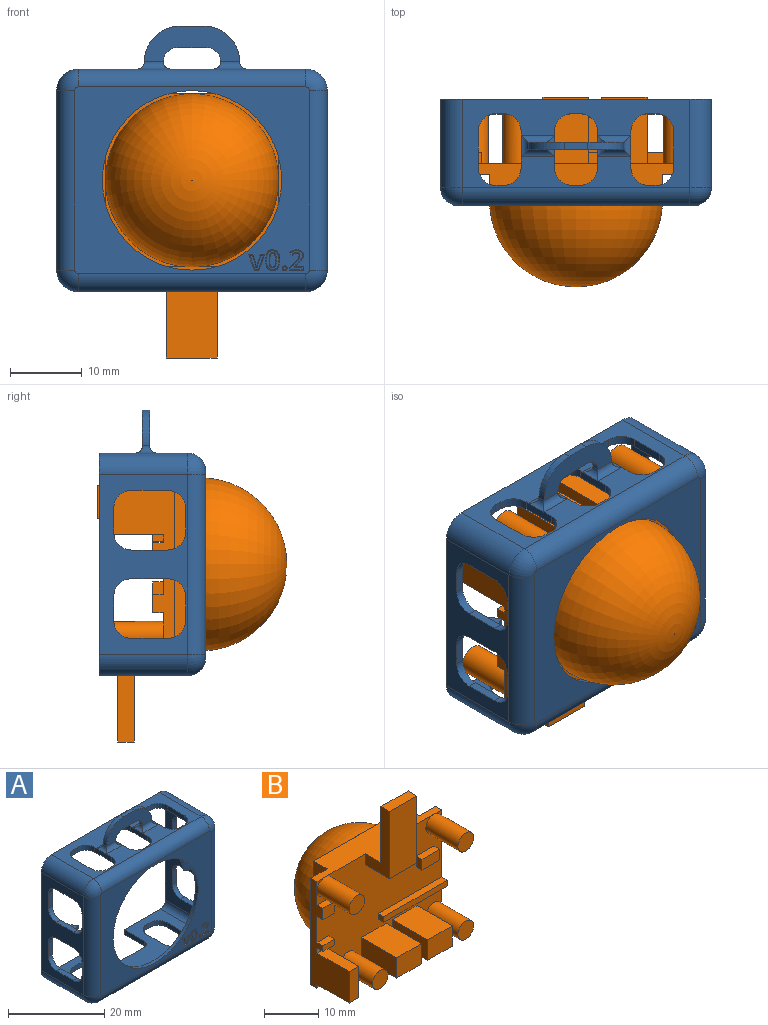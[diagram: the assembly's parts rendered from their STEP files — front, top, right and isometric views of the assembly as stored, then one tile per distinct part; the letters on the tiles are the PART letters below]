
ASSEMBLY  parts=2 mates=2
PART A: 200 faces, bbox 37.9x15x37.2 mm
  f0: plane 32.86x26.2mm, normal (0,-1,0), area 350.2mm2, adj f18,f129,f130,f131,f132,f133,f134,f135
  f1: plane 31.7x12.3mm, normal (0,0,1), area 198.1mm2, adj f9,f10,f17,f65,f66,f67,f68,f69
  f2: plane 32.3x12.5mm, normal (0,0,1), area 217.7mm2, adj f12,f13,f17,f20,f21,f22,f23,f24
  f3: plane 31.7x12.3mm, normal (0,0,-1), area 203.9mm2, adj f11,f16,f17,f20,f21,f22,f23,f24
  f4: plane 32.3x12.5mm, normal (0,0,-1), area 239.8mm2, adj f14,f15,f17,f65,f66,f67,f68,f69
  f5: plane 25.64x12.5mm, normal (1,0,0), area 156.8mm2, adj f13,f14,f17,f25,f26,f27,f28,f49
  f6: plane 25.04x12.3mm, normal (1,0,0), area 152.3mm2, adj f9,f16,f17,f33,f34,f35,f36,f37
  f7: plane 25.04x12.3mm, normal (-1,0,0), area 152.3mm2, adj f10,f11,f17,f49,f50,f51,f52,f53
  f8: plane 25.64x12.5mm, normal (-1,0,0), area 156.8mm2, adj f12,f15,f17,f29,f30,f31,f32,f33
  f9: cylinder r=3mm len=12.3mm, axis (0,-1,0), area 58mm2, adj f1,f6,f17,f134
  f10: cylinder r=3mm len=12.3mm, axis (0,-1,0), area 58mm2, adj f1,f7,f17,f130
  f11: cylinder r=3mm len=12.3mm, axis (0,-1,0), area 58mm2, adj f3,f7,f17,f131
  f12: cylinder r=1.5mm len=12.5mm, axis (0,-1,0), area 29.5mm2, adj f2,f8,f17,f126
  f13: cylinder r=1.5mm len=12.5mm, axis (0,-1,0), area 29.5mm2, adj f2,f5,f17,f127
  f14: cylinder r=1.5mm len=12.5mm, axis (0,-1,0), area 29.5mm2, adj f4,f5,f17,f123
  f15: cylinder r=1.5mm len=12.5mm, axis (0,-1,0), area 29.5mm2, adj f4,f8,f17,f122
  f16: cylinder r=3mm len=12.3mm, axis (0,-1,0), area 58mm2, adj f3,f6,f17,f135
  f17: plane 37.7x31.04mm, normal (0,1,0), area 140.8mm2, adj f1,f2,f3,f4,f5,f6,f7,f8
  f18: cylinder r=12.5mm len=25mm, axis (0,1,0), area 62.8mm2, adj f0,f19
  f19: plane 32.3x25.64mm, normal (0,1,0), area 337.3mm2, adj f18,f121,f124,f125,f128
  f20: plane 5.9x1.2mm, normal (-1,0,0), area 7.1mm2, adj f2,f3,f17,f21
  f21: cylinder r=1.5mm len=1.5mm, axis (0,0,-1), area 2.8mm2, adj f2,f3,f20,f22
  f22: plane 7.5x1.2mm, normal (0,1,0), area 9mm2, adj f2,f3,f21,f23
  f23: cylinder r=1.5mm len=1.5mm, axis (0,0,-1), area 2.8mm2, adj f2,f3,f22,f24
  f24: plane 5.9x1.2mm, normal (1,0,0), area 7.1mm2, adj f2,f3,f17,f23
  f25: plane 2.2x2mm, normal (0.41,-0.91,0), area 4.8mm2, adj f5,f26,f27,f28
  f26: plane 3x2.2mm, normal (0.81,0.59,0), area 7.4mm2, adj f5,f25,f27,f28
  f27: plane 4x2.2mm, normal (0,0,-1), area 4.4mm2, adj f5,f25,f26
  f28: plane 4x2.2mm, normal (0,0,1), area 4.4mm2, adj f5,f25,f26
  f29: plane 3x2.2mm, normal (-0.81,0.59,0), area 7.4mm2, adj f8,f30,f31,f32
  f30: plane 2.2x2mm, normal (-0.41,-0.91,0), area 4.8mm2, adj f8,f29,f31,f32
  f31: plane 4x2.2mm, normal (0,0,1), area 4.4mm2, adj f8,f29,f30
  f32: plane 4x2.2mm, normal (0,0,-1), area 4.4mm2, adj f8,f29,f30
  f33: plane 3.32x1.2mm, normal (0,-1,0), area 4mm2, adj f6,f8,f34,f40
  f34: cylinder r=2.5mm len=2.5mm, axis (1,0,0), area 4.7mm2, adj f6,f8,f33,f35
  f35: plane 5x1.2mm, normal (0,0,1), area 6mm2, adj f6,f8,f34,f36
  f36: cylinder r=2.5mm len=2.5mm, axis (1,0,0), area 4.7mm2, adj f6,f8,f35,f37
  f37: plane 3.32x1.2mm, normal (0,1,0), area 4mm2, adj f6,f8,f36,f38
  f38: cylinder r=2.5mm len=2.5mm, axis (1,0,0), area 4.7mm2, adj f6,f8,f37,f39
  f39: plane 5x1.2mm, normal (0,0,-1), area 6mm2, adj f6,f8,f38,f40
  f40: cylinder r=2.5mm len=2.5mm, axis (1,0,0), area 4.7mm2, adj f6,f8,f33,f39
  f41: cylinder r=2.5mm len=2.5mm, axis (1,0,0), area 4.7mm2, adj f6,f8,f42,f48
  f42: plane 3.32x1.2mm, normal (0,1,0), area 4mm2, adj f6,f8,f41,f43
  f43: cylinder r=2.5mm len=2.5mm, axis (1,0,0), area 4.7mm2, adj f6,f8,f42,f44
  f44: plane 5x1.2mm, normal (0,0,-1), area 6mm2, adj f6,f8,f43,f45
  f45: cylinder r=2.5mm len=2.5mm, axis (1,0,0), area 4.7mm2, adj f6,f8,f44,f46
  f46: plane 3.32x1.2mm, normal (0,-1,0), area 4mm2, adj f6,f8,f45,f47
  f47: cylinder r=2.5mm len=2.5mm, axis (1,0,0), area 4.7mm2, adj f6,f8,f46,f48
  f48: plane 5x1.2mm, normal (0,0,1), area 6mm2, adj f6,f8,f41,f47
  f49: cylinder r=2.5mm len=2.5mm, axis (1,0,0), area 4.7mm2, adj f5,f7,f50,f56
  f50: plane 5x1.2mm, normal (0,0,-1), area 6mm2, adj f5,f7,f49,f51
  f51: cylinder r=2.5mm len=2.5mm, axis (1,0,0), area 4.7mm2, adj f5,f7,f50,f52
  f52: plane 3.32x1.2mm, normal (0,1,0), area 4mm2, adj f5,f7,f51,f53
  f53: cylinder r=2.5mm len=2.5mm, axis (1,0,0), area 4.7mm2, adj f5,f7,f52,f54
  f54: plane 5x1.2mm, normal (0,0,1), area 6mm2, adj f5,f7,f53,f55
  f55: cylinder r=2.5mm len=2.5mm, axis (1,0,0), area 4.7mm2, adj f5,f7,f54,f56
  f56: plane 3.32x1.2mm, normal (0,-1,0), area 4mm2, adj f5,f7,f49,f55
  f57: plane 5x1.2mm, normal (0,0,1), area 6mm2, adj f5,f7,f58,f64
  f58: cylinder r=2.5mm len=2.5mm, axis (1,0,0), area 4.7mm2, adj f5,f7,f57,f59
  f59: plane 3.32x1.2mm, normal (0,-1,0), area 4mm2, adj f5,f7,f58,f60
  f60: cylinder r=2.5mm len=2.5mm, axis (1,0,0), area 4.7mm2, adj f5,f7,f59,f61
  f61: plane 5x1.2mm, normal (0,0,-1), area 6mm2, adj f5,f7,f60,f62
  f62: cylinder r=2.5mm len=2.5mm, axis (1,0,0), area 4.7mm2, adj f5,f7,f61,f63
  f63: plane 3.32x1.2mm, normal (0,1,0), area 4mm2, adj f5,f7,f62,f64
  f64: cylinder r=2.5mm len=2.5mm, axis (1,0,0), area 4.7mm2, adj f5,f7,f57,f63
  f65: cylinder r=2.5mm len=2.5mm, axis (0,0,-1), area 4.7mm2, adj f1,f4,f66,f72
  f66: plane 5x1.2mm, normal (1,0,0), area 6mm2, adj f1,f4,f65,f67,f116
  f67: cylinder r=2.5mm len=2.5mm, axis (0,0,-1), area 4.7mm2, adj f1,f4,f66,f68
  f68: plane 1.2x1mm, normal (0,1,0), area 1.2mm2, adj f1,f4,f67,f69
  f69: cylinder r=2.5mm len=2.5mm, axis (0,0,-1), area 4.7mm2, adj f1,f4,f68,f70
  f70: plane 5x1.2mm, normal (-1,0,0), area 6mm2, adj f1,f4,f69,f71
  f71: cylinder r=2.5mm len=2.5mm, axis (0,0,-1), area 4.7mm2, adj f1,f4,f70,f72
  f72: plane 1.2x1mm, normal (0,-1,0), area 1.2mm2, adj f1,f4,f65,f71
  f73: plane 1.2x1mm, normal (0,-1,0), area 1.2mm2, adj f1,f4,f74,f80
  f74: cylinder r=2.5mm len=2.5mm, axis (0,0,-1), area 4.7mm2, adj f1,f4,f73,f75
  f75: plane 5x1.2mm, normal (1,0,0), area 6mm2, adj f1,f4,f74,f76,f120
  f76: cylinder r=2.5mm len=2.5mm, axis (0,0,-1), area 4.7mm2, adj f1,f4,f75,f77
  f77: plane 1.2x1mm, normal (0,1,0), area 1.2mm2, adj f1,f4,f76,f78
  f78: cylinder r=2.5mm len=2.5mm, axis (0,0,-1), area 4.7mm2, adj f1,f4,f77,f79
  f79: plane 5x1.2mm, normal (-1,0,0), area 6mm2, adj f1,f4,f78,f80,f113
  f80: cylinder r=2.5mm len=2.5mm, axis (0,0,-1), area 4.7mm2, adj f1,f4,f73,f79
  f81: plane 5x1.2mm, normal (-1,0,0), area 6mm2, adj f1,f4,f82,f88,f117
  f82: cylinder r=2.5mm len=2.5mm, axis (0,0,-1), area 4.7mm2, adj f1,f4,f81,f83
  f83: plane 1.2x1mm, normal (0,-1,0), area 1.2mm2, adj f1,f4,f82,f84
  f84: cylinder r=2.5mm len=2.5mm, axis (0,0,-1), area 4.7mm2, adj f1,f4,f83,f85
  f85: plane 5x1.2mm, normal (1,0,0), area 6mm2, adj f1,f4,f84,f86
  f86: cylinder r=2.5mm len=2.5mm, axis (0,0,-1), area 4.7mm2, adj f1,f4,f85,f87
  f87: plane 1.2x1mm, normal (0,1,0), area 1.2mm2, adj f1,f4,f86,f88
  f88: cylinder r=2.5mm len=2.5mm, axis (0,0,-1), area 4.7mm2, adj f1,f4,f81,f87
  f89: plane 5x1.2mm, normal (-1,0,0), area 6mm2, adj f2,f3,f90,f96
  f90: cylinder r=2.5mm len=2.5mm, axis (0,0,1), area 4.7mm2, adj f2,f3,f89,f91
  f91: plane 1.2x1mm, normal (0,-1,0), area 1.2mm2, adj f2,f3,f90,f92
  f92: cylinder r=2.5mm len=2.5mm, axis (0,0,1), area 4.7mm2, adj f2,f3,f91,f93
  f93: plane 5x1.2mm, normal (1,0,0), area 6mm2, adj f2,f3,f92,f94
  f94: cylinder r=2.5mm len=2.5mm, axis (0,0,1), area 4.7mm2, adj f2,f3,f93,f95
  f95: plane 1.2x1mm, normal (0,1,0), area 1.2mm2, adj f2,f3,f94,f96
  f96: cylinder r=2.5mm len=2.5mm, axis (0,0,1), area 4.7mm2, adj f2,f3,f89,f95
  f97: cylinder r=2.5mm len=2.5mm, axis (0,0,1), area 4.7mm2, adj f2,f3,f98,f104
  f98: plane 5x1.2mm, normal (1,0,0), area 6mm2, adj f2,f3,f97,f99
  f99: cylinder r=2.5mm len=2.5mm, axis (0,0,1), area 4.7mm2, adj f2,f3,f98,f100
  f100: plane 1.2x1mm, normal (0,1,0), area 1.2mm2, adj f2,f3,f99,f101
  f101: cylinder r=2.5mm len=2.5mm, axis (0,0,1), area 4.7mm2, adj f2,f3,f100,f102
  f102: plane 5x1.2mm, normal (-1,0,0), area 6mm2, adj f2,f3,f101,f103
  f103: cylinder r=2.5mm len=2.5mm, axis (0,0,1), area 4.7mm2, adj f2,f3,f102,f104
  f104: plane 1.2x1mm, normal (0,-1,0), area 1.2mm2, adj f2,f3,f97,f103
  f105: cylinder r=5mm len=5mm, axis (0,1,0), area 7.9mm2, adj f106,f111,f112,f117
  f106: plane 3.3x1mm, normal (0,0,1), area 3.3mm2, adj f105,f107,f111,f112
  f107: cylinder r=5mm len=5mm, axis (0,1,0), area 7.9mm2, adj f106,f111,f112,f116
  f108: cylinder r=2mm len=2mm, axis (0,1,0), area 3.1mm2, adj f109,f111,f112,f113
  f109: plane 4x1mm, normal (0,0,-1), area 4mm2, adj f108,f110,f111,f112
  f110: cylinder r=2mm len=2mm, axis (0,1,0), area 3.1mm2, adj f109,f111,f112,f120
  f111: plane 13.3x5mm, normal (0,-1,0), area 41.5mm2, adj f105,f106,f107,f108,f109,f110,f114,f118
  f112: plane 13.3x5mm, normal (0,1,0), area 41.5mm2, adj f105,f106,f107,f108,f109,f110,f115,f119
  f113: cylinder r=1mm len=3mm, axis (0,-1,0), area 2.7mm2, adj f79,f108,f114,f115
  f114: cylinder r=1mm len=4.65mm, axis (1,0,0), area 5.3mm2, adj f1,f111,f113,f116
  f115: cylinder r=1mm len=4.65mm, axis (-1,0,0), area 5.3mm2, adj f1,f112,f113,f116
  f116: cylinder r=1mm len=3mm, axis (0,1,0), area 2.7mm2, adj f66,f107,f114,f115
  f117: cylinder r=1mm len=3mm, axis (0,-1,0), area 2.7mm2, adj f81,f105,f118,f119
  f118: cylinder r=1mm len=4.65mm, axis (-1,0,0), area 5.3mm2, adj f1,f111,f117,f120
  f119: cylinder r=1mm len=4.65mm, axis (1,0,0), area 5.3mm2, adj f1,f112,f117,f120
  f120: cylinder r=1mm len=3mm, axis (0,1,0), area 2.7mm2, adj f75,f110,f118,f119
  f121: cylinder r=1.5mm len=32.3mm, axis (1,0,0), area 76.1mm2, adj f4,f19,f122,f123
  f122: sphere r=1.5mm, area 3.5mm2, adj f15,f121,f124
  f123: sphere r=1.5mm, area 3.5mm2, adj f14,f121,f125
  f124: cylinder r=1.5mm len=25.64mm, axis (0,0,-1), area 60.4mm2, adj f8,f19,f122,f126
  f125: cylinder r=1.5mm len=25.64mm, axis (0,0,1), area 60.4mm2, adj f5,f19,f123,f127
  f126: sphere r=1.5mm, area 3.5mm2, adj f12,f124,f128
  f127: sphere r=1.5mm, area 3.5mm2, adj f13,f125,f128
  f128: cylinder r=1.5mm len=32.3mm, axis (-1,0,0), area 76.1mm2, adj f2,f19,f126,f127
  f129: cylinder r=2.5mm len=25.04mm, axis (0,0,-1), area 98.3mm2, adj f0,f7,f130,f131
  f130: torus R=0.5mm, axis (0,-1,0), area 12.9mm2, adj f0,f10,f129,f132
  f131: torus R=0.5mm, axis (0,-1,0), area 12.9mm2, adj f0,f11,f129,f133
  f132: cylinder r=2.5mm len=31.7mm, axis (-1,0,0), area 124.5mm2, adj f0,f1,f130,f134
  f133: cylinder r=2.5mm len=31.7mm, axis (1,0,0), area 124.5mm2, adj f0,f3,f131,f135
  f134: torus R=0.5mm, axis (0,-1,0), area 12.9mm2, adj f0,f9,f132,f136
  f135: torus R=0.5mm, axis (0,-1,0), area 12.9mm2, adj f0,f16,f133,f136
  f136: cylinder r=2.5mm len=25.04mm, axis (0,0,1), area 98.3mm2, adj f0,f6,f134,f135
  f137: bspline ~1.08x0.36mm, area 0.3mm2, adj f0,f138,f152,f153
  f138: bspline ~0.73x0.45mm, area 0.2mm2, adj f0,f137,f139,f153
  f139: bspline ~0.74x0.43mm, area 0.2mm2, adj f0,f138,f140,f153
  f140: bspline ~1.09x0.35mm, area 0.3mm2, adj f0,f139,f141,f153
  f141: bspline ~1.07x0.36mm, area 0.3mm2, adj f0,f140,f142,f153
  f142: bspline ~0.73x0.44mm, area 0.2mm2, adj f0,f141,f143,f153
  f143: bspline ~0.74x0.43mm, area 0.2mm2, adj f0,f142,f152,f153
  f144: bspline ~0.79x0.24mm, area 0.2mm2, adj f145,f151,f153,f154
  f145: bspline ~0.43x0.36mm, area 0.1mm2, adj f144,f146,f153,f154
  f146: bspline ~0.43x0.36mm, area 0.1mm2, adj f145,f147,f153,f154
  f147: bspline ~0.79x0.24mm, area 0.2mm2, adj f146,f148,f153,f154
  f148: bspline ~0.79x0.24mm, area 0.2mm2, adj f147,f149,f153,f154
  f149: bspline ~0.43x0.36mm, area 0.1mm2, adj f148,f150,f153,f154
  f150: bspline ~0.43x0.36mm, area 0.1mm2, adj f149,f151,f153,f154
  f151: bspline ~0.79x0.24mm, area 0.2mm2, adj f144,f150,f153,f154
  f152: bspline ~1.09x0.36mm, area 0.3mm2, adj f0,f137,f143,f153
  f153: plane 2.83x1.91mm, normal (0,-1,0), area 2mm2, adj f137,f138,f139,f140,f141,f142,f143,f144
  f154: plane 2.06x0.92mm, normal (0,-1,0), area 1.3mm2, adj f144,f145,f146,f147,f148,f149,f150,f151
  f155: plane 0.5x0.2mm, normal (-0.87,-0.5,0), area 0.1mm2, adj f0,f156,f178,f179
  f156: plane 1.34x0.2mm, normal (0,-0.5,-0.87), area 0.3mm2, adj f0,f155,f157,f179
  f157: plane 0.2x0.19mm, normal (-0.87,-0.5,0), area 0mm2, adj f0,f156,f158,f179
  f158: plane 0.49x0.44mm, normal (-0.59,-0.5,0.63), area 0.1mm2, adj f0,f157,f159,f179
  f159: bspline ~0.6x0.6mm, area 0.2mm2, adj f0,f158,f160,f179
  f160: bspline ~0.4x0.32mm, area 0.1mm2, adj f0,f159,f161,f179
  f161: bspline ~0.36x0.24mm, area 0.1mm2, adj f0,f160,f162,f179
  f162: bspline ~0.39x0.24mm, area 0.1mm2, adj f0,f161,f163,f179
  f163: bspline ~0.37x0.34mm, area 0.1mm2, adj f0,f162,f164,f179
  f164: bspline ~0.46x0.24mm, area 0.1mm2, adj f0,f163,f165,f179
  f165: bspline ~0.36x0.24mm, area 0.1mm2, adj f0,f164,f166,f179
  f166: bspline ~0.33x0.24mm, area 0.1mm2, adj f0,f165,f167,f179
  f167: bspline ~0.41x0.35mm, area 0.1mm2, adj f0,f166,f168,f179
  f168: plane 0.47x0.43mm, normal (0.66,-0.5,0.56), area 0.1mm2, adj f0,f167,f169,f179
  f169: bspline ~0.41x0.34mm, area 0.1mm2, adj f0,f168,f170,f179
  f170: bspline ~0.38x0.24mm, area 0.1mm2, adj f0,f169,f171,f179
  f171: bspline ~0.34x0.24mm, area 0.1mm2, adj f0,f170,f172,f179
  f172: bspline ~0.36x0.24mm, area 0.1mm2, adj f0,f171,f173,f179
  f173: bspline ~0.27x0.24mm, area 0.1mm2, adj f0,f172,f174,f179
  f174: bspline ~0.31x0.27mm, area 0.1mm2, adj f0,f173,f175,f179
  f175: bspline ~0.55x0.52mm, area 0.1mm2, adj f0,f174,f176,f179
  f176: plane 0.8x0.78mm, normal (0.62,-0.5,-0.61), area 0.2mm2, adj f0,f175,f177,f179
  f177: plane 0.41x0.2mm, normal (0.87,-0.5,0), area 0.1mm2, adj f0,f176,f178,f179
  f178: plane 1.96x0.2mm, normal (0,-0.5,0.87), area 0.4mm2, adj f0,f155,f177,f179
  f179: plane 2.74x1.86mm, normal (0,-1,0), area 1.5mm2, adj f155,f156,f157,f158,f159,f160,f161,f162
  f180: bspline ~0.24x0.24mm, area 0.1mm2, adj f0,f181,f187,f188
  f181: bspline ~0.25x0.24mm, area 0.1mm2, adj f0,f180,f182,f188
  f182: bspline ~0.25x0.24mm, area 0.1mm2, adj f0,f181,f183,f188
  f183: bspline ~0.24x0.24mm, area 0mm2, adj f0,f182,f184,f188
  f184: bspline ~0.24x0.24mm, area 0.1mm2, adj f0,f183,f185,f188
  f185: bspline ~0.25x0.24mm, area 0.1mm2, adj f0,f184,f186,f188
  f186: bspline ~0.25x0.24mm, area 0.1mm2, adj f0,f185,f187,f188
  f187: bspline ~0.24x0.24mm, area 0.1mm2, adj f0,f180,f186,f188
  f188: plane 0.48x0.46mm, normal (0,-1,0), area 0.2mm2, adj f180,f181,f182,f183,f184,f185,f186,f187
  f189: plane 0.6x0.2mm, normal (0,-0.5,0.87), area 0.1mm2, adj f0,f190,f198,f199
  f190: plane 2.14x0.9mm, normal (-0.81,-0.5,0.31), area 0.5mm2, adj f0,f189,f191,f199
  f191: plane 0.61x0.2mm, normal (0,-0.5,-0.87), area 0.1mm2, adj f0,f190,f192,f199
  f192: plane 1.26x0.5mm, normal (0.82,-0.5,-0.28), area 0.3mm2, adj f0,f191,f193,f199
  f193: bspline ~0.56x0.24mm, area 0.1mm2, adj f0,f192,f194,f199
  f194: plane 0.24x0.21mm, normal (0,-0.5,-0.87), area 0mm2, adj f0,f193,f195,f199
  f195: bspline ~0.56x0.24mm, area 0.1mm2, adj f0,f194,f196,f199
  f196: plane 1.26x0.5mm, normal (-0.82,-0.5,-0.28), area 0.3mm2, adj f0,f195,f197,f199
  f197: plane 0.61x0.2mm, normal (0,-0.5,-0.87), area 0.1mm2, adj f0,f196,f198,f199
  f198: plane 2.14x0.9mm, normal (0.81,-0.5,0.31), area 0.5mm2, adj f0,f189,f197,f199
  f199: plane 1.98x1.97mm, normal (0,-1,0), area 1.2mm2, adj f189,f190,f191,f192,f193,f194,f195,f196
PART B: 64 faces, bbox 32.6x26.4x36.8 mm
  f0: plane 32.6x9.15mm, normal (0,0,1), area 165.3mm2, adj f1,f2,f3,f5,f6,f7,f8,f9
  f1: plane 32.6x24.1mm, normal (0,-1,0), area 591.1mm2, adj f0,f8,f9,f10,f19,f21,f23,f25
  f2: plane 2.05x2.05mm, normal (0,-1,0), area 0.9mm2, adj f0,f8,f21
  f3: plane 2.05x2.05mm, normal (0,-1,0), area 0.9mm2, adj f0,f9,f19
  f4: plane 12.05x12.05mm, normal (0,1,0), area 31.2mm2, adj f10,f13,f16
  f5: plane 12.05x12.05mm, normal (0,1,0), area 31.2mm2, adj f0,f13,f16
  f6: plane 12.05x12.05mm, normal (0,1,0), area 31.2mm2, adj f0,f14,f16
  f7: plane 24.1x4.25mm, normal (0,1,0), area 102.4mm2, adj f0,f8,f10,f13
  f8: plane 24.1x3.1mm, normal (1,0,0), area 40.5mm2, adj f0,f1,f2,f7,f10,f12,f46,f47
  f9: plane 24.1x10mm, normal (-1,0,0), area 104mm2, adj f0,f1,f3,f10,f11,f27,f29,f30
  f10: plane 32.6x5.1mm, normal (0,0,-1), area 136.5mm2, adj f1,f4,f7,f8,f9,f11,f12,f13
  f11: plane 24.1x4.25mm, normal (0,1,0), area 102.4mm2, adj f0,f9,f10,f14
  f12: plane 2.05x2.05mm, normal (0,-1,0), area 0.9mm2, adj f8,f10,f23
  f13: plane 24.1x3.5mm, normal (1,0,0), area 84.4mm2, adj f0,f4,f5,f7,f10
  f14: plane 24.1x3.5mm, normal (-1,0,0), area 84.4mm2, adj f0,f6,f10,f11,f15
  f15: plane 12.05x12.05mm, normal (0,1,0), area 31.2mm2, adj f10,f14,f16
  f16: cylinder r=12.05mm len=24.1mm, axis (0,-1,0), area 7.6mm2, adj f4,f5,f6,f15,f18
  f17: plane 0.1x0.1mm, normal (0,1,0), area 0mm2, adj f18
  f18: torus R=0.05mm, axis (0,-1,0), area 910.7mm2, adj f16,f17
  f19: cylinder r=2.05mm len=8.4mm, axis (0,1,0), area 108.2mm2, adj f1,f3,f20
  f20: plane 4.1x4.1mm, normal (0,-1,0), area 13.2mm2, adj f19
  f21: cylinder r=2.05mm len=8.4mm, axis (0,1,0), area 108.2mm2, adj f1,f2,f22
  f22: plane 4.1x4.1mm, normal (0,-1,0), area 13.2mm2, adj f21
  f23: cylinder r=2.05mm len=8.4mm, axis (0,1,0), area 108.2mm2, adj f1,f12,f24
  f24: plane 4.1x4.1mm, normal (0,-1,0), area 13.2mm2, adj f23
  f25: cylinder r=2.05mm len=8.4mm, axis (0,1,0), area 108.2mm2, adj f1,f26
  f26: plane 4.1x4.1mm, normal (0,-1,0), area 13.2mm2, adj f25
  f27: plane 8.4x2.5mm, normal (0,0,-1), area 21mm2, adj f1,f9,f28,f30
  f28: plane 8.4x7.1mm, normal (1,0,0), area 59.6mm2, adj f1,f27,f29,f30
  f29: plane 8.4x2.5mm, normal (0,0,1), area 21mm2, adj f1,f9,f28,f30
  f30: plane 7.1x2.5mm, normal (0,-1,0), area 17.7mm2, adj f9,f27,f28,f29
  f31: plane 9.2x4.6mm, normal (-1,0,0), area 42.3mm2, adj f1,f32,f34,f35
  f32: plane 9.2x6.4mm, normal (0,0,-1), area 58.9mm2, adj f1,f31,f33,f35
  f33: plane 9.2x4.6mm, normal (1,0,0), area 42.3mm2, adj f1,f32,f34,f35
  f34: plane 9.2x6.4mm, normal (0,0,1), area 58.9mm2, adj f1,f31,f33,f35
  f35: plane 6.4x4.6mm, normal (0,-1,0), area 29.4mm2, adj f31,f32,f33,f34
  f36: plane 9.2x4.6mm, normal (-1,0,0), area 42.3mm2, adj f1,f37,f39,f40
  f37: plane 9.2x6.4mm, normal (0,0,-1), area 58.9mm2, adj f1,f36,f38,f40
  f38: plane 9.2x4.6mm, normal (1,0,0), area 42.3mm2, adj f1,f37,f39,f40
  f39: plane 9.2x6.4mm, normal (0,0,1), area 58.9mm2, adj f1,f36,f38,f40
  f40: plane 6.4x4.6mm, normal (0,-1,0), area 29.4mm2, adj f36,f37,f38,f39
  f41: plane 2.4x1.5mm, normal (-1,0,0), area 3.6mm2, adj f1,f42,f44,f45
  f42: plane 4.6x1.5mm, normal (0,0,-1), area 6.9mm2, adj f1,f41,f43,f45
  f43: plane 2.4x1.5mm, normal (1,0,0), area 3.6mm2, adj f1,f42,f44,f45
  f44: plane 4.6x1.5mm, normal (0,0,1), area 6.9mm2, adj f1,f41,f43,f45
  f45: plane 4.6x2.4mm, normal (0,-1,0), area 11mm2, adj f41,f42,f43,f44
  f46: plane 16.6x1.5mm, normal (0,0,-1), area 24.9mm2, adj f1,f8,f48,f49
  f47: plane 16.6x1.5mm, normal (0,0,1), area 24.9mm2, adj f1,f8,f48,f49
  f48: plane 1.5x1.3mm, normal (-1,0,0), area 1.9mm2, adj f1,f46,f47,f49
  f49: plane 16.6x1.3mm, normal (0,-1,0), area 21.6mm2, adj f8,f46,f47,f48
  f50: plane 3.1x1.5mm, normal (0,0,1), area 4.6mm2, adj f1,f9,f52,f53
  f51: plane 3.1x1.5mm, normal (0,0,-1), area 4.6mm2, adj f1,f9,f52,f53
  f52: plane 2.6x1.5mm, normal (1,0,0), area 3.9mm2, adj f1,f50,f51,f53
  f53: plane 3.1x2.6mm, normal (0,-1,0), area 8.1mm2, adj f9,f50,f51,f52
  f54: plane 3.1x1.5mm, normal (0,0,-1), area 4.6mm2, adj f1,f9,f55,f57
  f55: plane 1.5x1.3mm, normal (1,0,0), area 2mm2, adj f1,f54,f56,f57
  f56: plane 3.1x1.5mm, normal (0,0,1), area 4.6mm2, adj f1,f9,f55,f57
  f57: plane 3.1x1.3mm, normal (0,-1,0), area 4mm2, adj f9,f54,f55,f56
  f58: plane 15.2x6.35mm, normal (-1,0,0), area 45.1mm2, adj f0,f1,f59,f61,f62,f63
  f59: plane 7.1x6.35mm, normal (0,0,-1), area 45.1mm2, adj f1,f58,f60,f61
  f60: plane 15.2x6.35mm, normal (1,0,0), area 45.1mm2, adj f0,f1,f59,f61,f62,f63
  f61: plane 15.2x7.1mm, normal (0,-1,0), area 107.9mm2, adj f58,f59,f60,f63
  f62: plane 12.7x7.1mm, normal (0,1,0), area 90.2mm2, adj f0,f58,f60,f63
  f63: plane 7.1x2.3mm, normal (0,0,1), area 16.3mm2, adj f58,f60,f61,f62
PLACE A t=(-9.36,0.4,-9.36)mm
PLACE B rot(axis=(1,0,0),180deg) t=(-9.36,5.5,-9.36)mm
MATE cylindrical A.f18 <-> B.f16  axis (0,1,0) through (-9.36,0,-9.36)mm
MATE planar B.f4 <-> A.f18  axis (0,-1,0) through (0,0.4,0)mm
